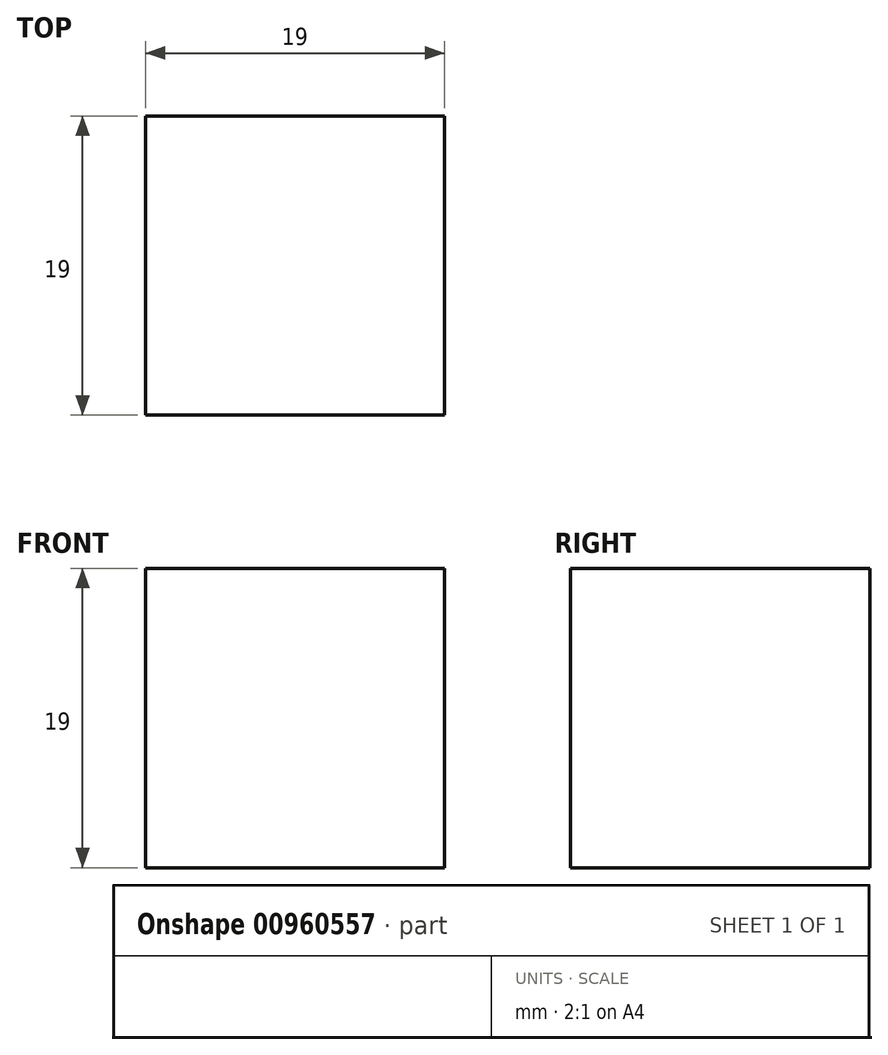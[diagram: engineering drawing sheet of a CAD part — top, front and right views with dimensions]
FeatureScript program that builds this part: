
annotation { "Feature Type Name" : "Feature", "Feature Type Description" : "" }
export const myFeature = defineFeature(function(context is Context, id is Id, definition is map)
    precondition{}
    {
        {
            var Q0;
            Q0=qCreatedBy(makeId("Top.planeOp"),FACE);
            var sketch = newSketch(context, id + "F0", { "sketchPlane" : qUnion([Q0])});
            skLineSegment(sketch, "E0.bottom", {"start": v(9.5, 9.5) * mm, "end": v(-9.5, 9.5) * mm});
            skLineSegment(sketch, "E0.top", {"start": v(9.5, -9.5) * mm, "end": v(-9.5, -9.5) * mm});
            skLineSegment(sketch, "E0.left", {"start": v(9.5, 9.5) * mm, "end": v(9.5, -9.5) * mm});
            skLineSegment(sketch, "E0.right", {"start": v(-9.5, 9.5) * mm, "end": v(-9.5, -9.5) * mm});
            skPoint(sketch, "E0.middle", {"position": v(0, 0) * mm});
            skSolve(sketch);
        }
        {
            var Q0;
            Q0 = qSketchRegion(id + "F0", true);
            extrude(context, id + "F1", {"entities" : qUnion([Q0]), "endBound" : BoundingType.SYMMETRIC, "depth" : 19 * mm, "offsetDistance" : 25 * mm});
        }
    });
